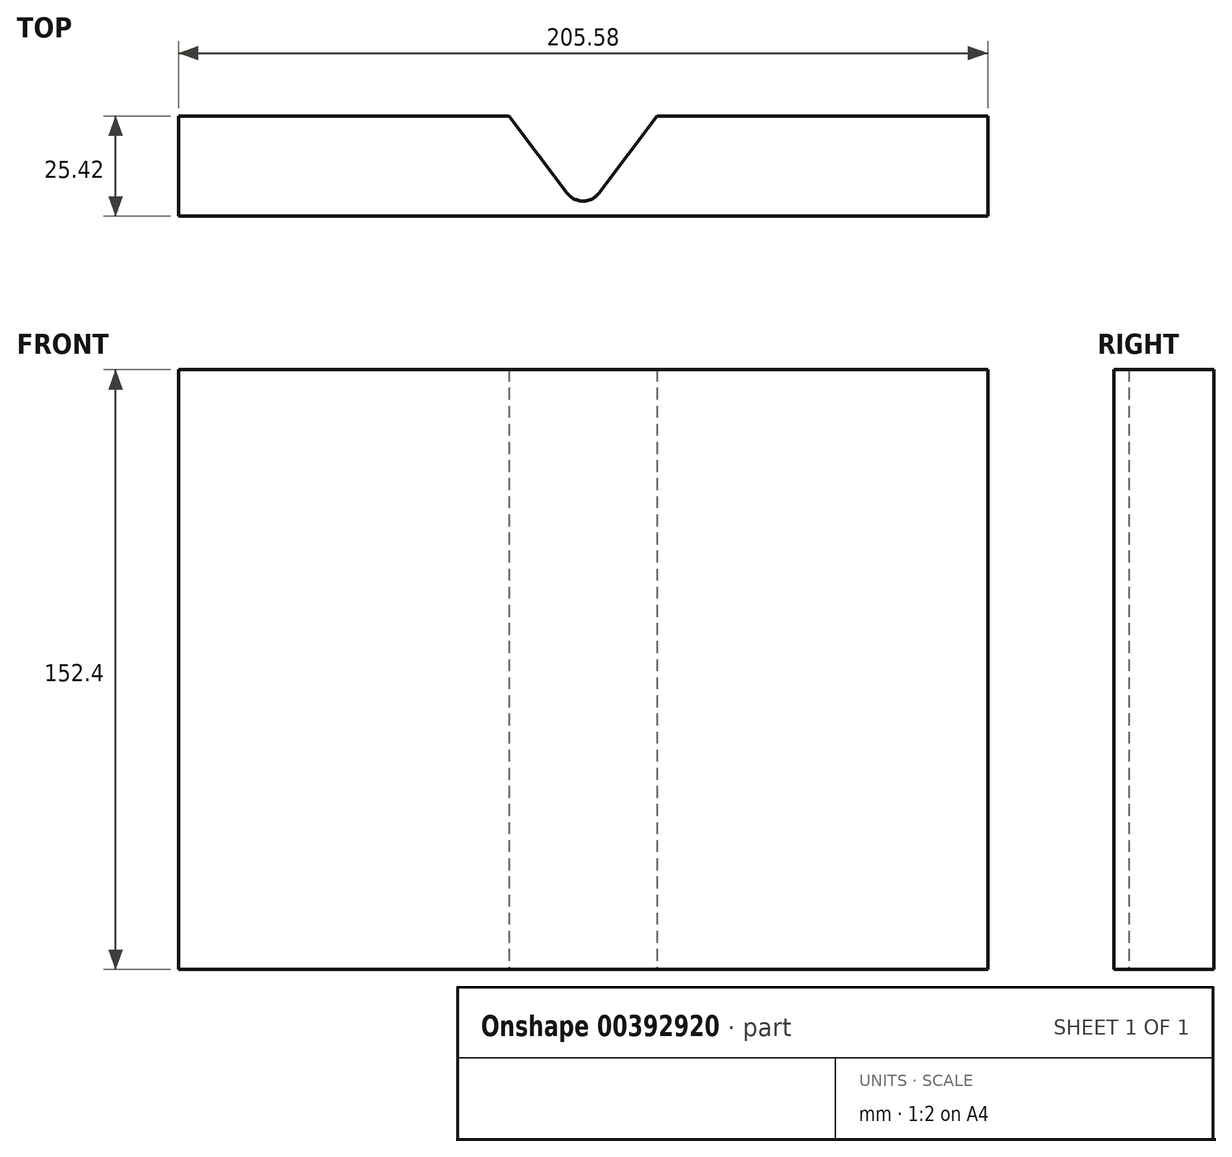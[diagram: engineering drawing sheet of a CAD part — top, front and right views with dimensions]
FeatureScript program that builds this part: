
annotation { "Feature Type Name" : "Feature", "Feature Type Description" : "" }
export const myFeature = defineFeature(function(context is Context, id is Id, definition is map)
    precondition{}
    {
        {
            var Q0;
            Q0=qCreatedBy(makeId("Top.planeOp"),FACE);
            var sketch = newSketch(context, id + "F0", { "sketchPlane" : qUnion([Q0])});
            skLineSegment(sketch, "E0.bottom", {"start": v(0, 0) * mm, "end": v(-26.6, 0) * mm});
            skLineSegment(sketch, "E0.top", {"start": v(0, 6.63) * mm, "end": v(-26.6, 6.63) * mm});
            skLineSegment(sketch, "E0.left", {"start": v(0, 0) * mm, "end": v(0, 6.63) * mm});
            skLineSegment(sketch, "E0.right", {"start": v(-26.6, 0) * mm, "end": v(-26.6, 6.63) * mm});
            skSolve(sketch);
        }
        {
            var Q0;
            Q0=makeQuery(id+"F0.imprint","IMPRINT",FACE,{"disambiguationData":[TD([[makeQuery(id+"F0.imprint","IMPRINT",EDGE,{"derivedFrom":sQuery(id+"F0.wireOp",EDGE,"E0.bottom")}),-1.0]])]});
            extrude(context, id + "F1", {"entities" : qUnion([Q0]), "depth" : 152.4 * mm});
        }
        {
            var Q0;
            Q0=makeQuery(id+"F1.opExtrude","SWEPT_FACE",FACE,{"disambiguationData":[OSD([sQuery(id+"F0.wireOp",EDGE,"E0.right")])]});
            extrude(context, id + "F2", {"entities" : qUnion([Q0]), "operationType" : NewBodyOperationType.ADD, "depth" : 76.2 * mm});
        }
        {
            var Q0;
            {var subQ0=sQuery(id+"F0.wireOp",EDGE,"E0.top");Q0=makeQuery(id+"F2.boolean.opBoolean","MERGE",FACE,{"derivedFrom":[makeQuery(id+"F1.opExtrude","SWEPT_FACE",FACE,{"disambiguationData":[OSD([subQ0])]}),makeQuery(id+"F2.opExtrude","SWEPT_FACE",FACE,{"disambiguationData":[OSD([subQ0,sQuery(id+"F0.wireOp",EDGE,"E0.right")])]})]});}
            extrude(context, id + "F3", {"entities" : qUnion([Q0]), "operationType" : NewBodyOperationType.ADD, "depth" : 18.8 * mm});
        }
        {
            var Q0;
            Q0=makeQuery(id+"F3.opExtrude","CAP_EDGE",EDGE,{"disambiguationData":[OSD([sQuery(id+"F0.wireOp",EDGE,"E0.top"),sQuery(id+"F0.wireOp",EDGE,"E0.left")])],"isStart":false});
            chamfer(context, id + "F4", {"entities" : qUnion([Q0]), "chamferType" : ChamferType.OFFSET_ANGLE, "width" : 18.8 * mm, "oppositeDirection" : false, "angle" : 53 * degree, "tangentPropagation" : true});
        }
        {
            var Q0;
            Q0=makeQuery(id+"F1.opExtrude","SWEPT_BODY",BODY,{"disambiguationData":[OSD([sQuery(id+"F0.wireOp",EDGE,"E0.bottom"),sQuery(id+"F0.wireOp",EDGE,"E0.top"),sQuery(id+"F0.wireOp",EDGE,"E0.left"),sQuery(id+"F0.wireOp",EDGE,"E0.right")])]});
            var Q1;
            Q1=qCreatedBy(makeId("Right.planeOp"),FACE);
            mirror(context, id + "F5", {"operationType" : NewBodyOperationType.ADD, "entities" : qUnion([Q0]), "mirrorPlane" : qUnion([Q1])});
        }
        {
            var Q0;
            {var subQ0=sQuery(id+"F0.wireOp",EDGE,"E0.left");var subQ1=sQuery(id+"F0.wireOp",EDGE,"E0.top");var subQ2=makeQuery(id+"F4.opChamfer","BLEND_EDGE",EDGE,{"blendedFrom":[makeQuery(id+"F3.opExtrude","CAP_EDGE",EDGE,{"disambiguationData":[OSD([subQ1,subQ0])],"isStart":false}),makeQuery(id+"F3.boolean.opBoolean","MERGE",FACE,{"derivedFrom":[makeQuery(id+"F1.opExtrude","SWEPT_FACE",FACE,{"disambiguationData":[OSD([subQ0])]}),makeQuery(id+"F3.opExtrude","SWEPT_FACE",FACE,{"disambiguationData":[OSD([subQ1,subQ0])]})]})],"blendedInto":[makeQuery(id+"F3.boolean.opBoolean","MERGE",FACE,{"derivedFrom":[makeQuery(id+"F1.opExtrude","SWEPT_FACE",FACE,{"disambiguationData":[OSD([subQ0])]}),makeQuery(id+"F3.opExtrude","SWEPT_FACE",FACE,{"disambiguationData":[OSD([subQ1,subQ0])]})]})]});Q0=makeQuery(id+"F5.boolean.opBoolean","MERGE",EDGE,{"derivedFrom":[subQ2,makeQuery(id+"F5.opPattern","COPY",EDGE,{"derivedFrom":subQ2,"instanceName":"1"})]});}
            fillet(context, id + "F6", {"entities" : qUnion([Q0]), "radius" : 5.08 * mm, "tangentPropagation" : true, "allowEdgeOverflow" : false});
        }
    });
